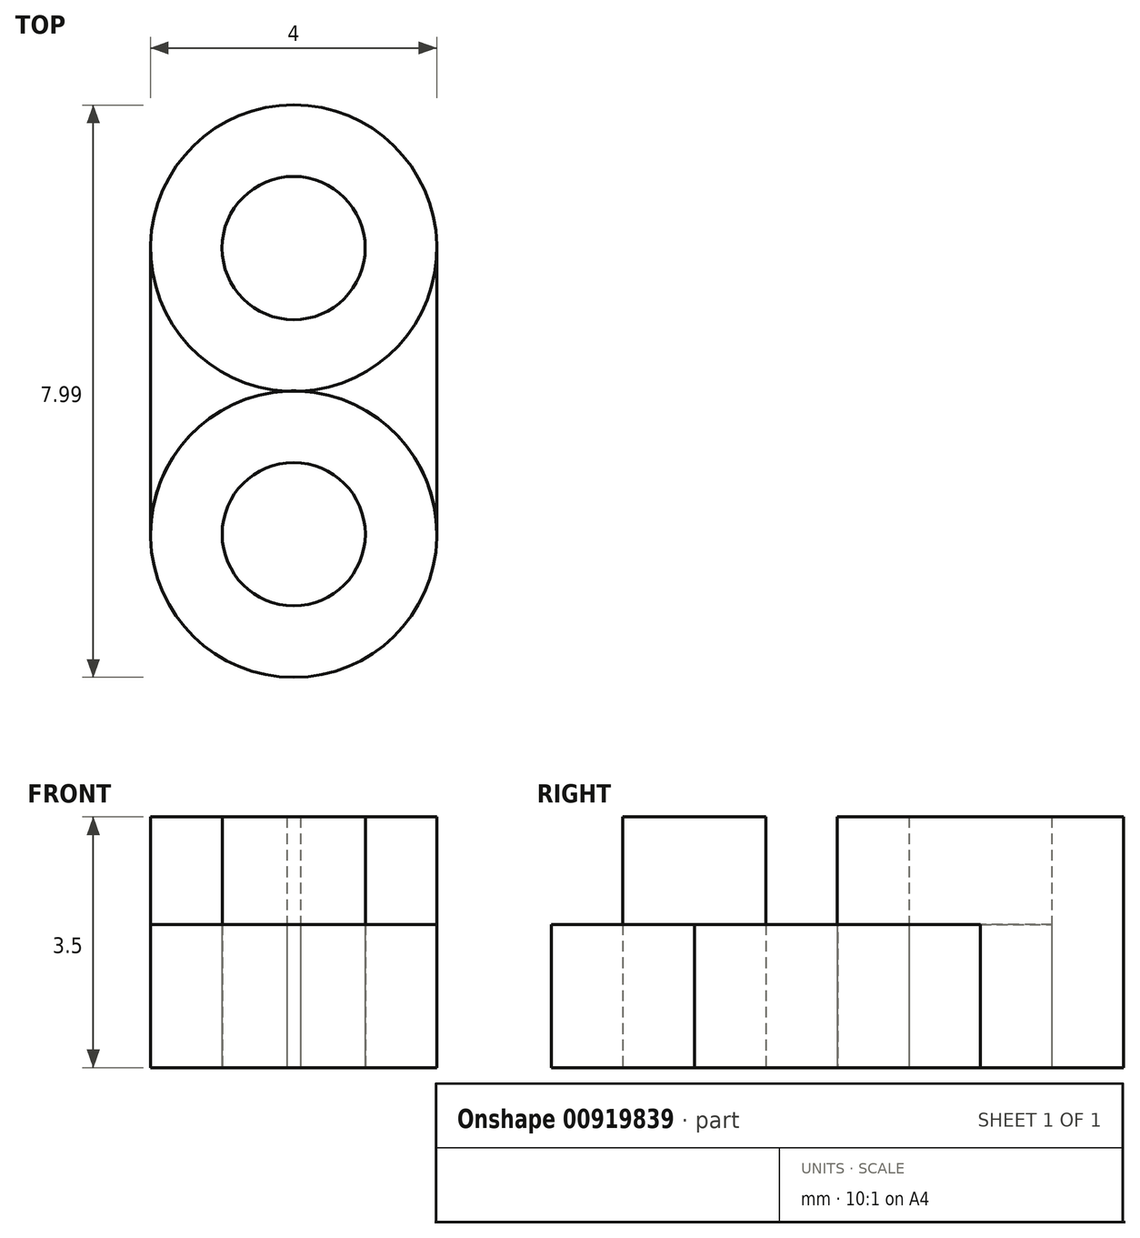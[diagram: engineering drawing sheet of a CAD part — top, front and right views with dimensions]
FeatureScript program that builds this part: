
annotation { "Feature Type Name" : "Feature", "Feature Type Description" : "" }
export const myFeature = defineFeature(function(context is Context, id is Id, definition is map)
    precondition{}
    {
        {
            var Q0;
            Q0=qCreatedBy(makeId("Top.planeOp"),FACE);
            var sketch = newSketch(context, id + "F0", { "sketchPlane" : qUnion([Q0])});
            skCircle(sketch, "E0", {"center": v(-2.4, -2.1) * mm, "radius": 1 * mm});
            skCircle(sketch, "E1.0", {"center": v(-2.4, -2.1) * mm, "radius": 2 * mm});
            skCircle(sketch, "E2.MirrorC", {"center": v(-2.4, 1.9) * mm, "radius": 2 * mm});
            skCircle(sketch, "E3.MirrorC", {"center": v(-2.4, 1.9) * mm, "radius": 1 * mm});
            skLineSegment(sketch, "E4", {"start": v(-4.4, 1.9) * mm, "end": v(-4.4, -2.1) * mm});
            skLineSegment(sketch, "E5", {"start": v(-0.4, 1.9) * mm, "end": v(-0.4, -2.1) * mm});
            skSolve(sketch);
        }
        {
            var Q0;
            Q0=makeQuery(id+"F0.imprint","IMPRINT",FACE,{"disambiguationData":[TD([[makeQuery(id+"F0.imprint","IMPRINT",EDGE,{"derivedFrom":sQuery(id+"F0.wireOp",EDGE,"E3.MirrorC")}),-1.0]])]});
            var Q1;
            Q1=makeQuery(id+"F0.imprint","IMPRINT",FACE,{"disambiguationData":[TD([[makeQuery(id+"F0.imprint","IMPRINT",EDGE,{"derivedFrom":sQuery(id+"F0.wireOp",EDGE,"0ae744ae-f55b-40fc-a7b3-f8d2a7c8a9f70.MirrorC")}),1.0]])]});
            var Q2;
            Q2=makeQuery(id+"F0.imprint","IMPRINT",FACE,{"disambiguationData":[TD([[makeQuery(id+"F0.imprint","IMPRINT",EDGE,{"derivedFrom":sQuery(id+"F0.wireOp",EDGE,"d17cf97a-931a-448d-8b80-c103a7b4494f0.MirrorC")}),-1.0]])]});
            var Q3;
            Q3=makeQuery(id+"F0.imprint","IMPRINT",FACE,{"disambiguationData":[TD([[makeQuery(id+"F0.imprint","IMPRINT",EDGE,{"derivedFrom":sQuery(id+"F0.wireOp",EDGE,"E0")}),1.0]])]});
            extrude(context, id + "F1", {"entities" : qUnion([Q0, Q1, Q2, Q3]), "depth" : 3.5 * mm, "offsetDistance" : 25 * mm});
        }
        {
            var Q0;
            Q0=makeQuery(id+"F0.imprint","IMPRINT",FACE,{"disambiguationData":[TD([[makeQuery(id+"F0.imprint","IMPRINT",EDGE,{"derivedFrom":sQuery(id+"F0.wireOp",EDGE,"E0")}),-1.0]])]});
            var Q1;
            Q1=makeQuery(id+"F0.imprint","IMPRINT",FACE,{"disambiguationData":[TD([[makeQuery(id+"F0.imprint","IMPRINT",EDGE,{"derivedFrom":sQuery(id+"F0.wireOp",EDGE,"d17cf97a-931a-448d-8b80-c103a7b4494f0.MirrorC")}),1.0]])]});
            var Q2;
            Q2=makeQuery(id+"F0.imprint","IMPRINT",FACE,{"disambiguationData":[TD([[makeQuery(id+"F0.imprint","IMPRINT",EDGE,{"derivedFrom":sQuery(id+"F0.wireOp",EDGE,"0ae744ae-f55b-40fc-a7b3-f8d2a7c8a9f70.MirrorC")}),-1.0]])]});
            var Q3;
            Q3=makeQuery(id+"F0.imprint","IMPRINT",FACE,{"disambiguationData":[TD([[makeQuery(id+"F0.imprint","IMPRINT",EDGE,{"derivedFrom":sQuery(id+"F0.wireOp",EDGE,"E3.MirrorC")}),1.0]])]});
            extrude(context, id + "F2", {"entities" : qUnion([Q0, Q1, Q2, Q3]), "depth" : 2 * mm, "offsetDistance" : 25 * mm});
        }
        {
            var Q0;
            {var subQ0=sQuery(id+"F0.wireOp",EDGE,"8708e262-4cf4-405b-86c6-c2c9bbcd91690.MirrorC");var subQ1=sQuery(id+"F0.wireOp",EDGE,"E1.0");var subQ2=makeQuery(id+"F0.imprint","INTERSECT",VERTEX,{"derivedFrom":[subQ1,subQ0]});Q0=makeQuery(id+"F0.imprint","IMPRINT",FACE,{"disambiguationData":[TD([[makeQuery(id+"F0.imprint","IMPRINT",EDGE,{"disambiguationData":[TD([[subQ2,-1.0]])],"derivedFrom":subQ1}),-1.0]])]});}
            extrude(context, id + "F3", {"entities" : qUnion([Q0]), "depth" : 2 * mm, "offsetDistance" : 25 * mm});
        }
    });
